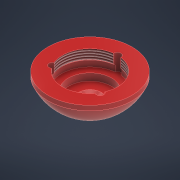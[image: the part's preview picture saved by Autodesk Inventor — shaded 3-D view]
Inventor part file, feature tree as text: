
AUTODESK INVENTOR PART (.ipt)
format: ipt  version: 2022 (Build 260153000, 153)  size: 366,592 bytes
history: native  units: mm
features: sketch x3, hole x2, other x1, revolve x1, pattern_circular x1
ambient origin geometry x8: Origin, YZ Plane, XZ Plane, XY Plane, X Axis, Y Axis, Z Axis, Center Point
bodies: Solid1 (feature_tree)
feature tree (8):
  other  "Anode"
  revolve  "Revolution1"  [1 undecoded]
  hole  "Hole1"  [1 undecoded]
  hole  "Hole2"  [1 undecoded]
  pattern_circular  "Circular Pattern1"  [2 undecoded]
  sketch  "Sketch1"  dims[d3=26.121296mm d7=24.99546mm]
  sketch  "Sketch2"  dims[d9=35.0mm d10=62.0mm]
  sketch  "Sketch3"  dims[d18=21.546564mm d19=14.0mm d26=19.0mm d27=1.0mm d34=22.0mm d38=135.0deg d39=2.0mm d41=2.0mm d42=60.0deg d44=24.0mm d45=360.0deg d54=11.831025mm d57=22.917468mm d58=5.0mm d59=4.0mm d60=2.0mm d61=90.0deg d62=5.0mm d63=0.0mm d65=3.0mm d66=12.0mm d67=4.0mm d68=2.0mm d69=90.0deg d70=6.0mm d71=0.0mm d72=30.0mm d73=360.0deg d82=18.0mm d83=10.0mm d86=7.0mm d87=3.5mm d90=150.0deg]
note: 5 required parameter values undecoded (feature->parameter linkage not recoverable at this tier; creation-order binding heuristic only, values carry confidence <= 0.55)